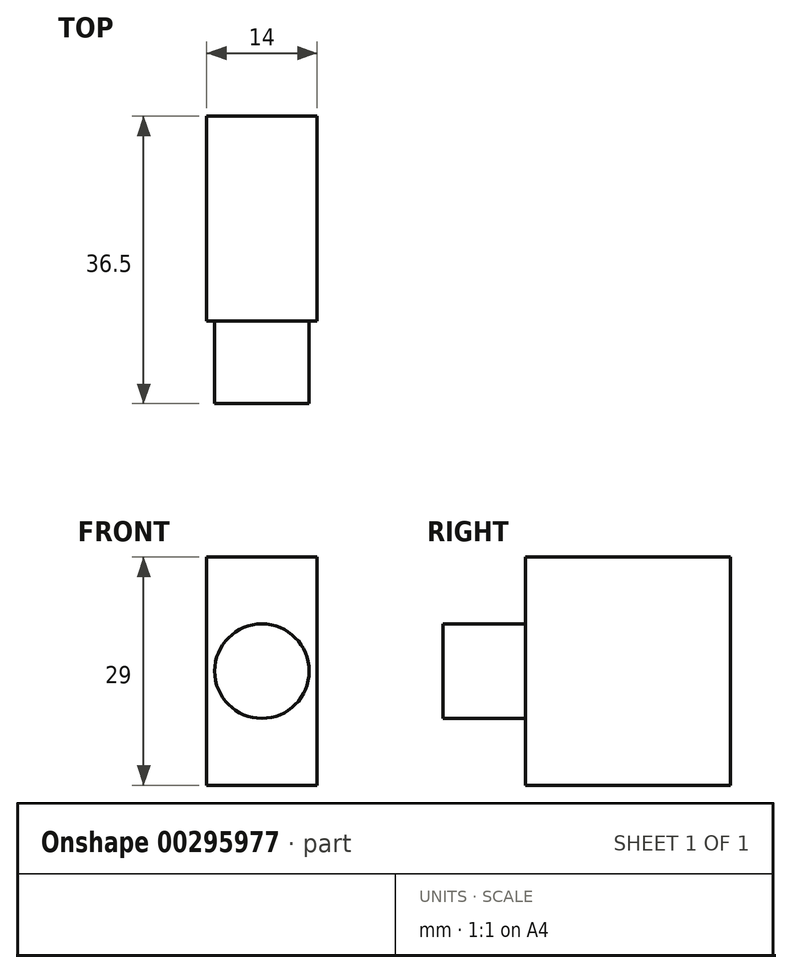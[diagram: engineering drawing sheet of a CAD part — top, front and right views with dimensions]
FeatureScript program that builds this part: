
annotation { "Feature Type Name" : "Feature", "Feature Type Description" : "" }
export const myFeature = defineFeature(function(context is Context, id is Id, definition is map)
    precondition{}
    {
        {
            var Q0;
            Q0=qCreatedBy(makeId("Front.planeOp"),FACE);
            var sketch = newSketch(context, id + "F0", { "sketchPlane" : qUnion([Q0])});
            skLineSegment(sketch, "E0.bottom", {"start": v(7, -14.5) * mm, "end": v(-7, -14.5) * mm});
            skLineSegment(sketch, "E0.top", {"start": v(7, 14.5) * mm, "end": v(-7, 14.5) * mm});
            skLineSegment(sketch, "E0.left", {"start": v(7, -14.5) * mm, "end": v(7, 14.5) * mm});
            skLineSegment(sketch, "E0.right", {"start": v(-7, -14.5) * mm, "end": v(-7, 14.5) * mm});
            skPoint(sketch, "E0.middle", {"position": v(0, 0) * mm});
            skSolve(sketch);
        }
        {
            var Q0;
            Q0=makeQuery(id+"F0.imprint","IMPRINT",FACE,{"disambiguationData":[TD([[makeQuery(id+"F0.imprint","IMPRINT",EDGE,{"derivedFrom":sQuery(id+"F0.wireOp",EDGE,"E0.bottom")}),-1.0]])]});
            extrude(context, id + "F1", {"entities" : qUnion([Q0]), "depth" : 26 * mm, "offsetDistance" : 25 * mm});
        }
        {
            var Q0;
            Q0=makeQuery(id+"F1.opExtrude","CAP_FACE",FACE,{"disambiguationData":[OSD([sQuery(id+"F0.wireOp",EDGE,"E0.bottom"),sQuery(id+"F0.wireOp",EDGE,"E0.top"),sQuery(id+"F0.wireOp",EDGE,"E0.left"),sQuery(id+"F0.wireOp",EDGE,"E0.right")])],"isStart":false});
            var sketch = newSketch(context, id + "F2", { "sketchPlane" : qUnion([Q0])});
            skCircle(sketch, "E1", {"center": v(0, 0) * mm, "radius": 6 * mm});
            skSolve(sketch);
        }
        {
            var Q0;
            Q0=makeQuery(id+"F2.imprint","IMPRINT",FACE,{"disambiguationData":[TD([[makeQuery(id+"F2.imprint","IMPRINT",EDGE,{"derivedFrom":sQuery(id+"F2.wireOp",EDGE,"E1")}),1.0]])]});
            extrude(context, id + "F3", {"entities" : qUnion([Q0]), "operationType" : NewBodyOperationType.ADD, "depth" : 10.5 * mm, "offsetDistance" : 25 * mm});
        }
    });
